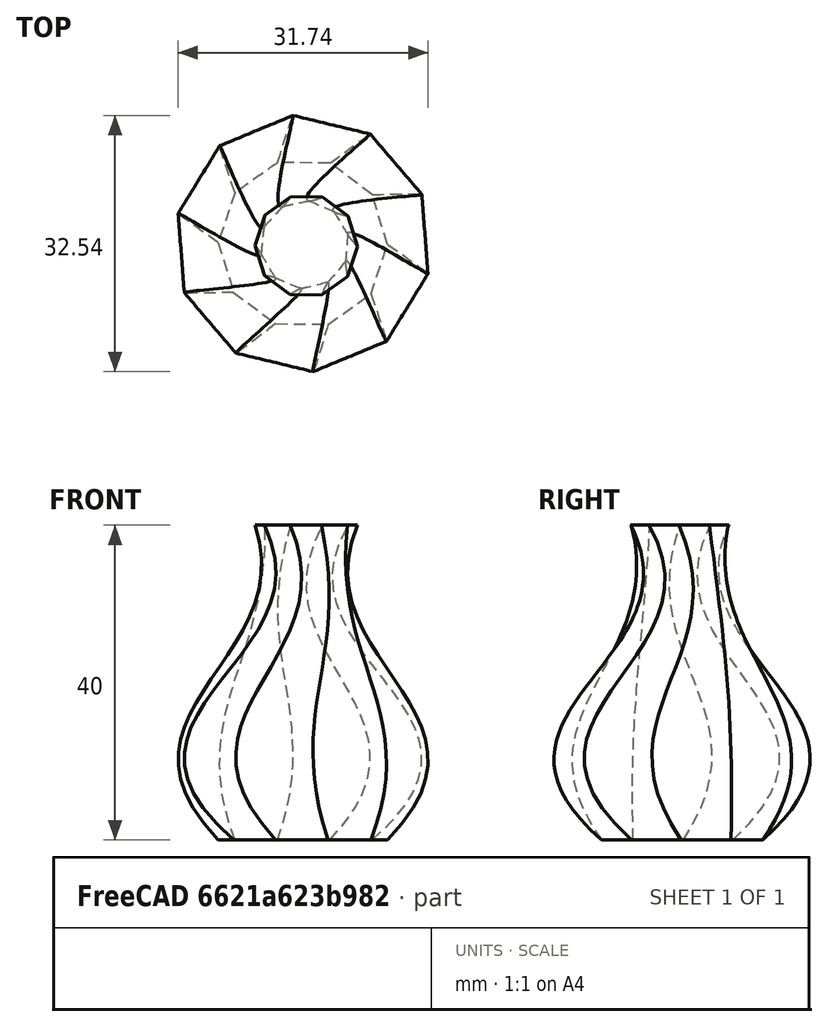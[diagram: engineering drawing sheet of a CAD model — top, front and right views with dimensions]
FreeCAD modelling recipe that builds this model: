
FCSTD DOCUMENT  (FreeCAD 0.18R4 (GitTag))
Label: Vase11
License: All rights reserved
LicenseURL: http://en.wikipedia.org/wiki/All_rights_reserved
objects: Sketcher::SketchObject×4, PartDesign::AdditiveLoft×1, PartDesign::Body×1
note: 7 computed .brp shape members not serialized (recipe doc carries the construction recipe); baked Part::Feature solids carry a one-line shape summary decoded from their .brp

FEATURE [Sketcher::SketchObject] Sketch  label="Verev"
  AttachmentOffset = pos=(0,0,40) rot=(0,0,1;0rad)
  MapMode = 5
  Placement = pos=(0,0,40) rot=(0,0,1;0rad)
  Support = -> [XY_Plane]
  sketch-geometry (11):
    g0: LineSegment StartX=5.74945 StartY=3.46941 StartZ=0 EndX=2.50984 EndY=5.87657 EndZ=0
    g1: LineSegment StartX=2.50984 StartY=5.87657 StartZ=0 EndX=-1.52595 EndY=5.9198 EndZ=0
    g2: LineSegment StartX=-1.52595 StartY=5.9198 StartZ=0 EndX=-4.81638 EndY=3.58261 EndZ=0
    g3: LineSegment StartX=-4.81638 StartY=3.58261 StartZ=0 EndX=-6.10463 EndY=-0.242296 EndZ=0
    g4: LineSegment StartX=-6.10463 StartY=-0.242296 StartZ=0 EndX=-4.89862 EndY=-4.09392 EndZ=0
    g5: LineSegment StartX=-4.89862 StartY=-4.09392 StartZ=0 EndX=-1.65902 EndY=-6.50108 EndZ=0
    g6: LineSegment StartX=-1.65902 StartY=-6.50108 StartZ=0 EndX=2.37677 EndY=-6.54431 EndZ=0
    g7: LineSegment StartX=2.37677 StartY=-6.54431 StartZ=0 EndX=5.66721 EndY=-4.20711 EndZ=0
    g8: LineSegment StartX=5.66721 StartY=-4.20711 StartZ=0 EndX=6.95545 EndY=-0.382212 EndZ=0
    g9: LineSegment StartX=6.95545 StartY=-0.382212 StartZ=0 EndX=5.74945 EndY=3.46941 EndZ=0
    g10: Circle [constr] CenterX=0.425412 CenterY=-0.312254 CenterZ=0 NormalX=0 NormalY=0 NormalZ=1 AngleXU=0 Radius=6.53042
  constraints (21):
    c: Coincident(g0,g1)
    c: Coincident(g1,g2)
    c: Coincident(g2,g3)
    c: Coincident(g3,g4)
    c: Coincident(g4,g5)
    c: Coincident(g5,g6)
    c: Coincident(g6,g7)
    c: Coincident(g7,g8)
    c: Coincident(g8,g9)
    c: Coincident(g9,g0)
    c: Equal(g0, g1-g9) x9
    c: PointOnObject(g0,g10)
    c: PointOnObject(g1,g10)
    c: PointOnObject(g2,g10)
    c: PointOnObject(g3,g10)
    c: PointOnObject(g4,g10)
    c: PointOnObject(g5,g10)
    c: PointOnObject(g6,g10)
    c: PointOnObject(g7,g10)
    c: PointOnObject(g8,g10)
    c: PointOnObject(g9,g10)
FEATURE [Sketcher::SketchObject] Sketch001
  AttachmentOffset = pos=(0,0,15) rot=(0,0,1;0rad)
  MapMode = 5
  Placement = pos=(0,0,15) rot=(0,0,1;0rad)
  Support = -> [XY_Plane]
  sketch-geometry (11):
    g0: LineSegment StartX=13.8826 StartY=6.05727 StartZ=0 EndX=7.67089 EndY=13.0604 EndZ=0
    g1: LineSegment StartX=7.67089 StartY=13.0604 StartZ=0 EndX=-1.47084 EndY=15.0749 EndZ=0
    g2: LineSegment StartX=-1.47084 StartY=15.0749 StartZ=0 EndX=-10.0508 EndY=11.3313 EndZ=0
    g3: LineSegment StartX=-10.0508 StartY=11.3313 StartZ=0 EndX=-14.7916 EndY=3.25956 EndZ=0
    g4: LineSegment StartX=-14.7916 StartY=3.25956 StartZ=0 EndX=-13.8826 EndY=-6.05727 EndZ=0
    g5: LineSegment StartX=-13.8826 StartY=-6.05727 StartZ=0 EndX=-7.67089 EndY=-13.0604 EndZ=0
    g6: LineSegment StartX=-7.67089 StartY=-13.0604 StartZ=0 EndX=1.47084 EndY=-15.0749 EndZ=0
    g7: LineSegment StartX=1.47084 StartY=-15.0749 StartZ=0 EndX=10.0508 EndY=-11.3313 EndZ=0
    g8: LineSegment StartX=10.0508 StartY=-11.3313 StartZ=0 EndX=14.7916 EndY=-3.25956 EndZ=0
    g9: LineSegment StartX=14.7916 StartY=-3.25956 StartZ=0 EndX=13.8826 EndY=6.05727 EndZ=0
    g10: Circle [constr] CenterX=0 CenterY=0 CenterZ=0 NormalX=0 NormalY=0 NormalZ=1 AngleXU=0 Radius=15.1465
  constraints (21):
    c: Coincident(g0,g1)
    c: Coincident(g1,g2)
    c: Coincident(g2,g3)
    c: Coincident(g3,g4)
    c: Coincident(g4,g5)
    c: Coincident(g5,g6)
    c: Coincident(g6,g7)
    c: Coincident(g7,g8)
    c: Coincident(g8,g9)
    c: Coincident(g9,g0)
    c: Equal(g0, g1-g9) x9
    c: PointOnObject(g0,g10)
    c: PointOnObject(g1,g10)
    c: PointOnObject(g2,g10)
    c: PointOnObject(g3,g10)
    c: PointOnObject(g4,g10)
    c: PointOnObject(g5,g10)
    c: PointOnObject(g6,g10)
    c: PointOnObject(g7,g10)
    c: PointOnObject(g8,g10)
    c: PointOnObject(g9,g10)
FEATURE [Sketcher::SketchObject] Sketch002
  AttachmentOffset = pos=(0,0,25) rot=(0,0,1;0rad)
  MapMode = 5
  Placement = pos=(0,0,25) rot=(0,0,1;0rad)
  Support = -> [XY_Plane]
  sketch-geometry (11):
    g0: LineSegment StartX=6.81033 StartY=5.27146 StartZ=0 EndX=2.41119 EndY=8.26771 EndZ=0
    g1: LineSegment StartX=2.41119 StartY=8.26771 StartZ=0 EndX=-2.90895 EndY=8.10598 EndZ=0
    g2: LineSegment StartX=-2.90895 StartY=8.10598 StartZ=0 EndX=-7.11796 EndY=4.84804 EndZ=0
    g3: LineSegment StartX=-7.11796 StartY=4.84804 StartZ=0 EndX=-8.60816 EndY=-0.261688 EndZ=0
    g4: LineSegment StartX=-8.60816 StartY=-0.261688 StartZ=0 EndX=-6.81033 EndY=-5.27146 EndZ=0
    g5: LineSegment StartX=-6.81033 StartY=-5.27146 StartZ=0 EndX=-2.41119 EndY=-8.26771 EndZ=0
    g6: LineSegment StartX=-2.41119 StartY=-8.26771 StartZ=0 EndX=2.90895 EndY=-8.10598 EndZ=0
    g7: LineSegment StartX=2.90895 StartY=-8.10598 StartZ=0 EndX=7.11796 EndY=-4.84804 EndZ=0
    g8: LineSegment StartX=7.11796 StartY=-4.84804 StartZ=0 EndX=8.60816 EndY=0.261688 EndZ=0
    g9: LineSegment StartX=8.60816 StartY=0.261688 StartZ=0 EndX=6.81033 EndY=5.27146 EndZ=0
    g10: Circle [constr] CenterX=0 CenterY=0 CenterZ=0 NormalX=0 NormalY=0 NormalZ=1 AngleXU=0 Radius=8.61214
  constraints (21):
    c: Coincident(g0,g1)
    c: Coincident(g1,g2)
    c: Coincident(g2,g3)
    c: Coincident(g3,g4)
    c: Coincident(g4,g5)
    c: Coincident(g5,g6)
    c: Coincident(g6,g7)
    c: Coincident(g7,g8)
    c: Coincident(g8,g9)
    c: Coincident(g9,g0)
    c: Equal(g0, g1-g9) x9
    c: PointOnObject(g0,g10)
    c: PointOnObject(g1,g10)
    c: PointOnObject(g2,g10)
    c: PointOnObject(g3,g10)
    c: PointOnObject(g4,g10)
    c: PointOnObject(g5,g10)
    c: PointOnObject(g6,g10)
    c: PointOnObject(g7,g10)
    c: PointOnObject(g8,g10)
    c: PointOnObject(g9,g10)
FEATURE [Sketcher::SketchObject] Sketch003
  MapMode = 5
  Support = -> [XY_Plane]
  sketch-geometry (11):
    g0: LineSegment StartX=-8.62888 StartY=6.43078 StartZ=0 EndX=-10.7608 EndY=0.130686 EndZ=0
    g1: LineSegment StartX=-10.7608 StartY=0.130686 StartZ=0 EndX=-8.78251 EndY=-6.21933 EndZ=0
    g2: LineSegment StartX=-8.78251 StartY=-6.21933 StartZ=0 EndX=-3.44957 EndY=-10.1938 EndZ=0
    g3: LineSegment StartX=-3.44957 StartY=-10.1938 StartZ=0 EndX=3.20099 EndY=-10.2745 EndZ=0
    g4: LineSegment StartX=3.20099 StartY=-10.2745 StartZ=0 EndX=8.62888 EndY=-6.43078 EndZ=0
    g5: LineSegment StartX=8.62888 StartY=-6.43078 StartZ=0 EndX=10.7608 EndY=-0.130686 EndZ=0
    g6: LineSegment StartX=10.7608 StartY=-0.130686 StartZ=0 EndX=8.78251 EndY=6.21933 EndZ=0
    g7: LineSegment StartX=8.78251 StartY=6.21933 StartZ=0 EndX=3.44957 EndY=10.1938 EndZ=0
    g8: LineSegment StartX=3.44957 StartY=10.1938 StartZ=0 EndX=-3.20099 EndY=10.2745 EndZ=0
    g9: LineSegment StartX=-3.20099 StartY=10.2745 StartZ=0 EndX=-8.62888 EndY=6.43078 EndZ=0
    g10: Circle [constr] CenterX=0 CenterY=0 CenterZ=0 NormalX=0 NormalY=0 NormalZ=1 AngleXU=0 Radius=10.7616
  constraints (21):
    c: Coincident(g0,g1)
    c: Coincident(g1,g2)
    c: Coincident(g2,g3)
    c: Coincident(g3,g4)
    c: Coincident(g4,g5)
    c: Coincident(g5,g6)
    c: Coincident(g6,g7)
    c: Coincident(g7,g8)
    c: Coincident(g8,g9)
    c: Coincident(g9,g0)
    c: Equal(g0, g1-g9) x9
    c: PointOnObject(g0,g10)
    c: PointOnObject(g1,g10)
    c: PointOnObject(g2,g10)
    c: PointOnObject(g3,g10)
    c: PointOnObject(g4,g10)
    c: PointOnObject(g5,g10)
    c: PointOnObject(g6,g10)
    c: PointOnObject(g7,g10)
    c: PointOnObject(g8,g10)
    c: PointOnObject(g9,g10)
FEATURE [PartDesign::AdditiveLoft] AdditiveLoft
  Closed = false
  Profile = -> Sketch003
  Ruled = false
  Sections = -> [Sketch001,Sketch002,Sketch]
FEATURE [PartDesign::Body] Body
  Group = -> [Sketch,Sketch001,Sketch002,Sketch003,AdditiveLoft]
  Origin = -> Origin
  Tip = -> AdditiveLoft
